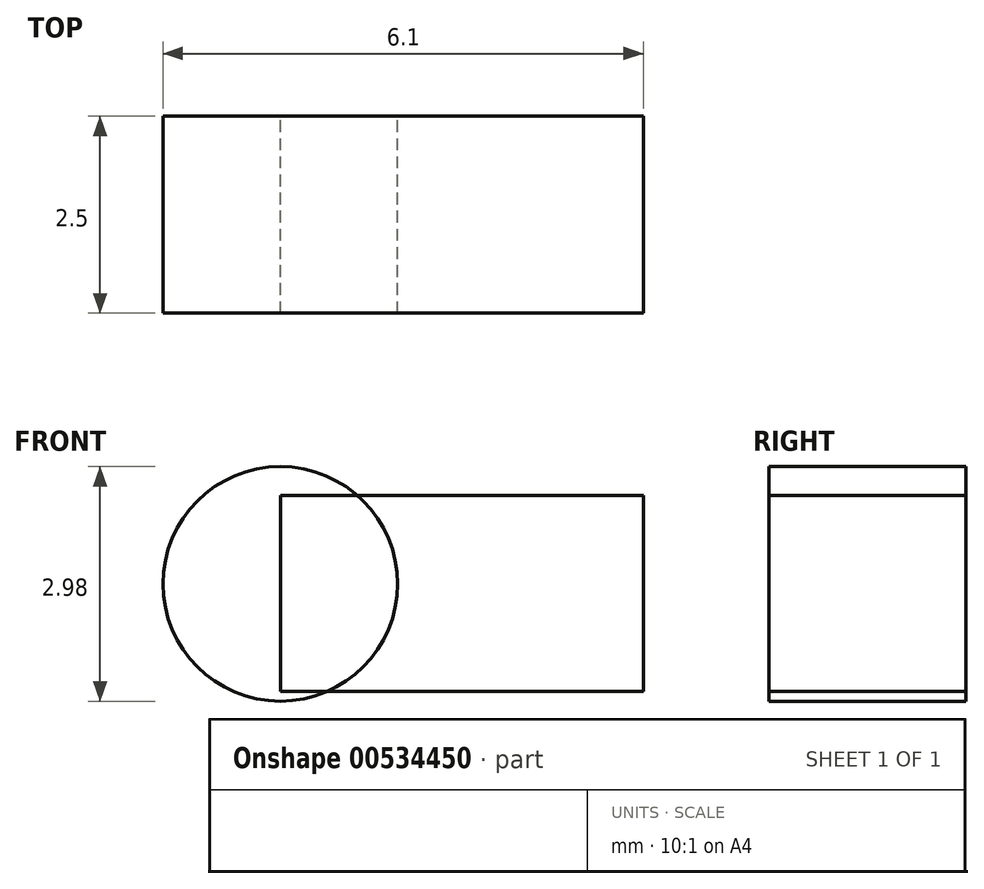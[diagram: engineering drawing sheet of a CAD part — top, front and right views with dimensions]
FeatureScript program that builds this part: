
annotation { "Feature Type Name" : "Feature", "Feature Type Description" : "" }
export const myFeature = defineFeature(function(context is Context, id is Id, definition is map)
    precondition{}
    {
        {
            var Q0;
            Q0=qCreatedBy(makeId("Front.planeOp"),FACE);
            var sketch = newSketch(context, id + "F0", { "sketchPlane" : qUnion([Q0])});
            skCircle(sketch, "E0", {"center": v(0, 0) * mm, "radius": 5.46 * mm});
            skCircle(sketch, "E1", {"center": v(0, 0) * mm, "radius": 4.04 * mm});
            skCircle(sketch, "E2", {"center": v(0, 0) * mm, "radius": 2.62 * mm});
            skCircle(sketch, "E3", {"center": v(0, 0) * mm, "radius": 1.68 * mm});
            skSolve(sketch);
        }
        {
            var Q0;
            Q0=makeQuery(id+"F0.imprint","IMPRINT",FACE,{"disambiguationData":[TD([[makeQuery(id+"F0.imprint","IMPRINT",EDGE,{"derivedFrom":sQuery(id+"F0.wireOp",EDGE,"E0")}),1.0]])]});
            var Q1;
            Q1=makeQuery(id+"F0.imprint","IMPRINT",FACE,{"disambiguationData":[TD([[makeQuery(id+"F0.imprint","IMPRINT",EDGE,{"derivedFrom":sQuery(id+"F0.wireOp",EDGE,"E2")}),1.0]])]});
            extrude(context, id + "F1", {"entities" : qUnion([Q0, Q1]), "depth" : 1.8 * mm, "offsetDistance" : 25 * mm});
        }
        {
            var Q0;
            Q0=makeQuery(id+"F1.opExtrude","SWEPT_BODY",BODY,{"disambiguationData":[OSD([sQuery(id+"F0.wireOp",EDGE,"E2"),sQuery(id+"F0.wireOp",EDGE,"E3")])]});
            var Q1;
            Q1=makeQuery(id+"F1.opExtrude","SWEPT_BODY",BODY,{"disambiguationData":[OSD([sQuery(id+"F0.wireOp",EDGE,"E0"),sQuery(id+"F0.wireOp",EDGE,"E1")])]});
            deleteBodies(context, id + "F2", {"entities" : qUnion([Q0, Q1])});
        }
        {
            var Q0;
            Q0=qCreatedBy(makeId("Front.planeOp"),FACE);
            var sketch = newSketch(context, id + "F3", { "sketchPlane" : qUnion([Q0])});
            skCircle(sketch, "E4", {"center": v(0, 0) * mm, "radius": 1.49 * mm});
            skSolve(sketch);
        }
        {
            var Q0;
            Q0 = qSketchRegion(id + "F3", true);
            extrude(context, id + "F4", {"entities" : qUnion([Q0]), "depth" : 2.5 * mm, "offsetDistance" : 25 * mm});
        }
        {
            var Q0;
            Q0=qCreatedBy(makeId("Front.planeOp"),FACE);
            var sketch = newSketch(context, id + "F5", { "sketchPlane" : qUnion([Q0])});
            skLineSegment(sketch, "E5.bottom", {"start": v(0, 1.13) * mm, "end": v(4.61, 1.13) * mm});
            skLineSegment(sketch, "E5.top", {"start": v(0, -1.36) * mm, "end": v(4.6, -1.36) * mm});
            skLineSegment(sketch, "E5.left", {"start": v(0, 1.13) * mm, "end": v(0, -1.36) * mm});
            skLineSegment(sketch, "E5.right", {"start": v(4.61, 1.13) * mm, "end": v(4.61, -1.36) * mm});
            skSolve(sketch);
        }
        {
            var Q0;
            Q0=makeQuery(id+"F5.imprint","IMPRINT",FACE,{"disambiguationData":[TD([[makeQuery(id+"F5.imprint","IMPRINT",EDGE,{"derivedFrom":sQuery(id+"F5.wireOp",EDGE,"E5.bottom")}),-1.0]])]});
            var Q1;
            Q1=makeQuery(id+"F4.opExtrude","CAP_FACE",FACE,{"disambiguationData":[OSD([sQuery(id+"F3.wireOp",EDGE,"E4")])],"isStart":false});
            extrude(context, id + "F6", {"entities" : qUnion([Q0]), "endBound" : BoundingType.UP_TO_SURFACE, "depth" : 25 * mm, "endBoundEntityFace" : qUnion([Q1]), "offsetDistance" : 25 * mm});
        }
    });
